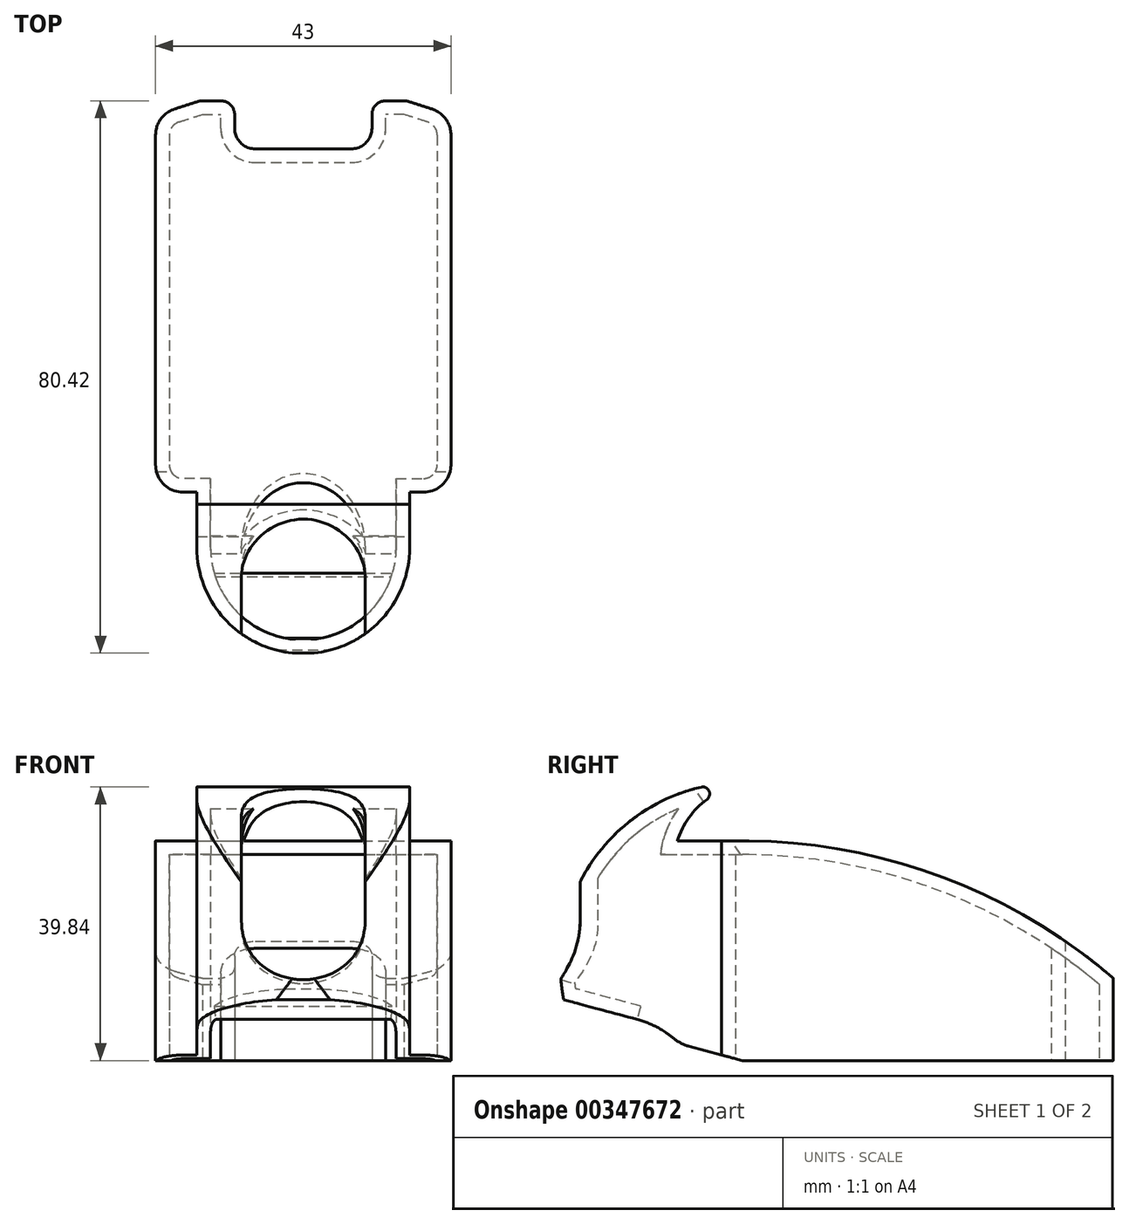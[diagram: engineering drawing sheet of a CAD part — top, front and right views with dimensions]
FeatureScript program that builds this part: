
annotation { "Feature Type Name" : "Feature", "Feature Type Description" : "" }
export const myFeature = defineFeature(function(context is Context, id is Id, definition is map)
    precondition{}
    {
        {
            var Q0;
            Q0=qCreatedBy(makeId("Top.planeOp"),FACE);
            var sketch = newSketch(context, id + "F0", { "sketchPlane" : qUnion([Q0])});
            skArc(sketch, "E0", {"start": v(-18.72, 27.8) * mm, "mid": v(-20.73, 26.36) * mm, "end": v(-21.5, 24) * mm});
            skArc(sketch, "E1.MirrorC", {"start": v(18.72, 27.8) * mm, "mid": v(20.73, 26.36) * mm, "end": v(21.5, 24) * mm});
            skArc(sketch, "E2.MirrorC", {"start": v(-17.5, -28) * mm, "mid": v(-20.33, -26.83) * mm, "end": v(-21.5, -24) * mm});
            skArc(sketch, "E3.MirrorC", {"start": v(17.5, -28) * mm, "mid": v(20.33, -26.83) * mm, "end": v(21.5, -24) * mm});
            skLineSegment(sketch, "E4", {"start": v(-21.5, 24) * mm, "end": v(-21.5, -24) * mm});
            skLineSegment(sketch, "E5", {"start": v(21.5, 24) * mm, "end": v(21.5, -24) * mm});
            skLineSegment(sketch, "E6", {"start": v(-7, 22) * mm, "end": v(7, 22) * mm});
            skLineSegment(sketch, "E7", {"start": v(-10, 25) * mm, "end": v(-10, 27) * mm});
            skLineSegment(sketch, "E8", {"start": v(10, 25) * mm, "end": v(10, 27) * mm});
            skPoint(sketch, "E9.visualSharp", {"position": v(-10, 22) * mm});
            skArc(sketch, "E9.filletArc", {"start": v(-10, 25) * mm, "mid": v(-9.12, 22.88) * mm, "end": v(-7, 22) * mm});
            skPoint(sketch, "E10.visualSharp", {"position": v(10, 22) * mm});
            skArc(sketch, "E10.filletArc", {"start": v(7, 22) * mm, "mid": v(9.12, 22.88) * mm, "end": v(10, 25) * mm});
            skLineSegment(sketch, "E11", {"start": v(-18.72, 27.8) * mm, "end": v(-15.3, 28.9) * mm});
            skLineSegment(sketch, "E12", {"start": v(-14.69, 29) * mm, "end": v(-12, 29) * mm});
            skLineSegment(sketch, "E13", {"start": v(18.72, 27.8) * mm, "end": v(15.3, 28.9) * mm});
            skLineSegment(sketch, "E14", {"start": v(14.69, 29) * mm, "end": v(12, 29) * mm});
            skPoint(sketch, "E15.visualSharp", {"position": v(-10, 29) * mm});
            skArc(sketch, "E15.filletArc", {"start": v(-10, 27) * mm, "mid": v(-10.59, 28.41) * mm, "end": v(-12, 29) * mm});
            skPoint(sketch, "E16.visualSharp", {"position": v(10, 29) * mm});
            skArc(sketch, "E16.filletArc", {"start": v(12, 29) * mm, "mid": v(10.59, 28.41) * mm, "end": v(10, 27) * mm});
            skPoint(sketch, "E17.visualSharp", {"position": v(-15, 29) * mm});
            skArc(sketch, "E17.filletArc", {"start": v(-14.69, 29) * mm, "mid": v(-15, 28.98) * mm, "end": v(-15.3, 28.9) * mm});
            skPoint(sketch, "E18.visualSharp", {"position": v(15, 29) * mm});
            skArc(sketch, "E18.filletArc", {"start": v(15.3, 28.9) * mm, "mid": v(15, 28.98) * mm, "end": v(14.69, 29) * mm});
            skLineSegment(sketch, "E19", {"start": v(-15.5, -28) * mm, "end": v(-15.5, -36) * mm});
            skLineSegment(sketch, "E20", {"start": v(15.5, -28) * mm, "end": v(15.5, -36) * mm});
            skLineSegment(sketch, "E21", {"start": v(-17.5, -28) * mm, "end": v(-15.5, -28) * mm});
            skLineSegment(sketch, "E22", {"start": v(17.5, -28) * mm, "end": v(15.5, -28) * mm});
            skArc(sketch, "E23", {"start": v(-15.5, -36) * mm, "mid": v(0, -51.5) * mm, "end": v(15.5, -36) * mm});
            skSolve(sketch);
        }
        {
            var Q0;
            Q0=makeQuery(id+"F0.imprint","IMPRINT",FACE,{"disambiguationData":[TD([[makeQuery(id+"F0.imprint","IMPRINT",EDGE,{"derivedFrom":sQuery(id+"F0.wireOp",EDGE,"E0")}),1.0]])]});
            extrude(context, id + "F1", {"entities" : qUnion([Q0]), "depth" : 32 * mm});
        }
        {
            var Q0;
            Q0=qCreatedBy(makeId("Right.planeOp"),FACE);
            var sketch = newSketch(context, id + "F2", { "sketchPlane" : qUnion([Q0])});
            skLineSegment(sketch, "E24", {"start": v(-25, 0) * mm, "end": v(-32.73, 2.07) * mm});
            skArc(sketch, "E25", {"start": v(-35, 3.25) * mm, "mid": v(-33.93, 2.54) * mm, "end": v(-32.73, 2.07) * mm});
            skArc(sketch, "E26", {"start": v(-35, 3.25) * mm, "mid": v(-37.51, 4.9) * mm, "end": v(-40.32, 6) * mm});
            skLineSegment(sketch, "E27", {"start": v(-40.32, 6) * mm, "end": v(-59, 11) * mm});
            skLineSegment(sketch, "E28", {"start": v(-59, 11) * mm, "end": v(-59, 0) * mm});
            skLineSegment(sketch, "E29", {"start": v(-59, 0) * mm, "end": v(-25, 0) * mm});
            skSolve(sketch);
        }
        {
            var Q0;
            Q0=makeQuery(id+"F2.imprint","IMPRINT",FACE,{"disambiguationData":[TD([[makeQuery(id+"F2.imprint","IMPRINT",EDGE,{"derivedFrom":sQuery(id+"F2.wireOp",EDGE,"E24")}),1.0]])]});
            extrude(context, id + "F3", {"entities" : qUnion([Q0]), "operationType" : NewBodyOperationType.REMOVE, "endBound" : BoundingType.SYMMETRIC, "oppositeDirection" : true, "depth" : 100 * mm});
        }
        {
            var Q0;
            Q0=qCreatedBy(makeId("Right.planeOp"),FACE);
            var sketch = newSketch(context, id + "F4", { "sketchPlane" : qUnion([Q0])});
            skArc(sketch, "E30", {"start": v(-43.47, 33) * mm, "mid": v(-50.57, 20.97) * mm, "end": v(-50.56, 7) * mm});
            skLineSegment(sketch, "E31", {"start": v(-43.47, 33) * mm, "end": v(-60, 33) * mm});
            skLineSegment(sketch, "E32", {"start": v(-60, 33) * mm, "end": v(-60, 7) * mm});
            skLineSegment(sketch, "E33", {"start": v(-60, 7) * mm, "end": v(-50.56, 7) * mm});
            skSolve(sketch);
        }
        {
            var Q0;
            Q0=makeQuery(id+"F4.imprint","IMPRINT",FACE,{"disambiguationData":[TD([[makeQuery(id+"F4.imprint","IMPRINT",EDGE,{"derivedFrom":sQuery(id+"F4.wireOp",EDGE,"E30")}),-1.0]])]});
            extrude(context, id + "F5", {"entities" : qUnion([Q0]), "operationType" : NewBodyOperationType.REMOVE, "endBound" : BoundingType.SYMMETRIC, "oppositeDirection" : true, "depth" : 100 * mm});
        }
        {
            var Q0;
            Q0=qCreatedBy(makeId("Right.planeOp"),FACE);
            var sketch = newSketch(context, id + "F6", { "sketchPlane" : qUnion([Q0])});
            skArc(sketch, "E34", {"start": v(29, 12) * mm, "mid": v(3.8, 26.84) * mm, "end": v(-25, 32) * mm});
            skLineSegment(sketch, "E35", {"start": v(29, 12) * mm, "end": v(29, 32) * mm});
            skLineSegment(sketch, "E36", {"start": v(29, 32) * mm, "end": v(-25, 32) * mm});
            skSolve(sketch);
        }
        {
            var Q0;
            Q0 = qSketchRegion(id + "F6", true);
            extrude(context, id + "F7", {"entities" : qUnion([Q0]), "operationType" : NewBodyOperationType.REMOVE, "endBound" : BoundingType.SYMMETRIC, "oppositeDirection" : true, "depth" : 50 * mm});
        }
        {
            var Q0;
            Q0=makeQuery(id+"F1.opExtrude","CAP_FACE",FACE,{"disambiguationData":[OSD([sQuery(id+"F0.wireOp",EDGE,"E0"),sQuery(id+"F0.wireOp",EDGE,"E1.MirrorC"),sQuery(id+"F0.wireOp",EDGE,"E2.MirrorC"),sQuery(id+"F0.wireOp",EDGE,"E3.MirrorC"),sQuery(id+"F0.wireOp",EDGE,"E4"),sQuery(id+"F0.wireOp",EDGE,"E5"),sQuery(id+"F0.wireOp",EDGE,"E6"),sQuery(id+"F0.wireOp",EDGE,"E7"),sQuery(id+"F0.wireOp",EDGE,"E8"),sQuery(id+"F0.wireOp",EDGE,"E9.filletArc"),sQuery(id+"F0.wireOp",EDGE,"E10.filletArc"),sQuery(id+"F0.wireOp",EDGE,"E11"),sQuery(id+"F0.wireOp",EDGE,"E12"),sQuery(id+"F0.wireOp",EDGE,"E13"),sQuery(id+"F0.wireOp",EDGE,"E14"),sQuery(id+"F0.wireOp",EDGE,"E15.filletArc"),sQuery(id+"F0.wireOp",EDGE,"E16.filletArc"),sQuery(id+"F0.wireOp",EDGE,"E17.filletArc"),sQuery(id+"F0.wireOp",EDGE,"E18.filletArc"),sQuery(id+"F0.wireOp",EDGE,"E19"),sQuery(id+"F0.wireOp",EDGE,"E20"),sQuery(id+"F0.wireOp",EDGE,"E21"),sQuery(id+"F0.wireOp",EDGE,"E22"),sQuery(id+"F0.wireOp",EDGE,"E23")])],"isStart":false});
            extrude(context, id + "F8", {"entities" : qUnion([Q0]), "operationType" : NewBodyOperationType.ADD, "depth" : 10 * mm});
        }
        {
            var Q0;
            Q0=qCreatedBy(makeId("Right.planeOp"),FACE);
            var sketch = newSketch(context, id + "F9", { "sketchPlane" : qUnion([Q0])});
            skArc(sketch, "E37", {"start": v(-30.97, 39.82) * mm, "mid": v(-38.3, 36.92) * mm, "end": v(-44.45, 32) * mm});
            skArc(sketch, "E38", {"start": v(-30.15, 38.04) * mm, "mid": v(-32.78, 35.36) * mm, "end": v(-34.45, 32) * mm});
            skLineSegment(sketch, "E39", {"start": v(-34.45, 32) * mm, "end": v(-44.45, 32) * mm, "construction": true});
            skLineSegment(sketch, "E40", {"start": v(-44.45, 32) * mm, "end": v(-25, 14) * mm, "construction": true});
            skPoint(sketch, "E41.visualSharp", {"position": v(-22.71, 40.4) * mm});
            skArc(sketch, "E41.filletArc", {"start": v(-30.15, 38.04) * mm, "mid": v(-29.84, 39.26) * mm, "end": v(-30.97, 39.82) * mm});
            skLineSegment(sketch, "E42", {"start": v(-34.45, 32) * mm, "end": v(-22.45, 32) * mm});
            skLineSegment(sketch, "E43", {"start": v(-22.45, 32) * mm, "end": v(-22.45, 44) * mm});
            skLineSegment(sketch, "E44", {"start": v(-22.45, 44) * mm, "end": v(-47.45, 44) * mm});
            skLineSegment(sketch, "E45", {"start": v(-47.45, 44) * mm, "end": v(-47.45, 32) * mm});
            skLineSegment(sketch, "E46", {"start": v(-47.45, 32) * mm, "end": v(-44.45, 32) * mm});
            skSolve(sketch);
        }
        {
            var Q0;
            Q0=makeQuery(id+"F9.imprint","IMPRINT",FACE,{"disambiguationData":[TD([[makeQuery(id+"F9.imprint","IMPRINT",EDGE,{"derivedFrom":sQuery(id+"F9.wireOp",EDGE,"E37")}),-1.0]])]});
            extrude(context, id + "F10", {"entities" : qUnion([Q0]), "operationType" : NewBodyOperationType.REMOVE, "endBound" : BoundingType.SYMMETRIC, "oppositeDirection" : true, "depth" : 50 * mm});
        }
        {
            var Q0;
            Q0=makeQuery(id+"F1.opExtrude","CAP_FACE",FACE,{"disambiguationData":[OSD([sQuery(id+"F0.wireOp",EDGE,"E0"),sQuery(id+"F0.wireOp",EDGE,"E1.MirrorC"),sQuery(id+"F0.wireOp",EDGE,"E2.MirrorC"),sQuery(id+"F0.wireOp",EDGE,"E3.MirrorC"),sQuery(id+"F0.wireOp",EDGE,"E4"),sQuery(id+"F0.wireOp",EDGE,"E5"),sQuery(id+"F0.wireOp",EDGE,"E6"),sQuery(id+"F0.wireOp",EDGE,"E7"),sQuery(id+"F0.wireOp",EDGE,"E8"),sQuery(id+"F0.wireOp",EDGE,"E9.filletArc"),sQuery(id+"F0.wireOp",EDGE,"E10.filletArc"),sQuery(id+"F0.wireOp",EDGE,"E11"),sQuery(id+"F0.wireOp",EDGE,"E12"),sQuery(id+"F0.wireOp",EDGE,"E13"),sQuery(id+"F0.wireOp",EDGE,"E14"),sQuery(id+"F0.wireOp",EDGE,"E15.filletArc"),sQuery(id+"F0.wireOp",EDGE,"E16.filletArc"),sQuery(id+"F0.wireOp",EDGE,"E17.filletArc"),sQuery(id+"F0.wireOp",EDGE,"E18.filletArc"),sQuery(id+"F0.wireOp",EDGE,"E19"),sQuery(id+"F0.wireOp",EDGE,"E20"),sQuery(id+"F0.wireOp",EDGE,"E21"),sQuery(id+"F0.wireOp",EDGE,"E22"),sQuery(id+"F0.wireOp",EDGE,"E23")])],"isStart":true});
            var Q1;
            Q1=makeQuery(id+"F3.boolean.opBoolean","COPY",FACE,{"derivedFrom":makeQuery(id+"F3.opExtrude","SWEPT_FACE",FACE,{"disambiguationData":[OSD([sQuery(id+"F2.wireOp",EDGE,"E24")])]})});
            var Q2;
            Q2=makeQuery(id+"F3.boolean.opBoolean","COPY",FACE,{"derivedFrom":makeQuery(id+"F3.opExtrude","SWEPT_FACE",FACE,{"disambiguationData":[OSD([sQuery(id+"F2.wireOp",EDGE,"E25")])]})});
            var Q3;
            Q3=makeQuery(id+"F3.boolean.opBoolean","COPY",FACE,{"derivedFrom":makeQuery(id+"F3.opExtrude","SWEPT_FACE",FACE,{"disambiguationData":[OSD([sQuery(id+"F2.wireOp",EDGE,"E26")])]})});
            shell(context, id + "F11", {"entities" : qUnion([Q0, Q1, Q2, Q3]), "thickness" : 2 * mm});
        }
        {
            var Q0;
            Q0=qCreatedBy(makeId("Right.planeOp"),FACE);
            var sketch = newSketch(context, id + "F12", { "sketchPlane" : qUnion([Q0])});
            skLineSegment(sketch, "E47", {"start": v(-25, 14) * mm, "end": v(-63.64, 24.35) * mm, "construction": true});
            skLineSegment(sketch, "E48", {"start": v(-25, 14) * mm, "end": v(-47.94, 46.77) * mm, "construction": true});
            skLineSegment(sketch, "E49", {"start": v(-25, 14) * mm, "end": v(-27.33, 5.3) * mm});
            skLineSegment(sketch, "E50", {"start": v(-27.33, 5.3) * mm, "end": v(-61.14, 14.37) * mm});
            skLineSegment(sketch, "E51", {"start": v(-25, 14) * mm, "end": v(-17.63, 19.16) * mm});
            skLineSegment(sketch, "E52", {"start": v(-17.63, 19.16) * mm, "end": v(-37.94, 48.17) * mm});
            skLineSegment(sketch, "E53", {"start": v(-37.94, 48.17) * mm, "end": v(-61.14, 14.37) * mm});
            skSolve(sketch);
        }
        {
            var Q0;
            Q0=makeQuery(id+"F12.imprint","IMPRINT",FACE,{"disambiguationData":[TD([[makeQuery(id+"F12.imprint","IMPRINT",EDGE,{"derivedFrom":sQuery(id+"F12.wireOp",EDGE,"E49")}),-1.0]])]});
            extrude(context, id + "F13", {"entities" : qUnion([Q0]), "operationType" : NewBodyOperationType.REMOVE, "endBound" : BoundingType.SYMMETRIC, "oppositeDirection" : true, "depth" : 18 * mm});
        }
        {
            var Q0;
            {var subQ0=sQuery(id+"F9.wireOp",EDGE,"E42");var subQ1=sQuery(id+"F12.wireOp",EDGE,"E52");Q0=makeQuery(id+"F13.boolean.opBoolean","COPY",EDGE,{"disambiguationData":[TD([makeQuery(id+"F10.boolean.opBoolean","COPY",FACE,{"derivedFrom":makeQuery(id+"F10.opExtrude","SWEPT_FACE",FACE,{"disambiguationData":[OSD([subQ0])]})})])],"derivedFrom":makeQuery(id+"F13.opExtrude","CAP_EDGE",EDGE,{"disambiguationData":[OSD([subQ1])],"isStart":false})});}
            var Q1;
            {var subQ0=sQuery(id+"F9.wireOp",EDGE,"E42");var subQ1=sQuery(id+"F12.wireOp",EDGE,"E52");Q1=makeQuery(id+"F13.boolean.opBoolean","COPY",EDGE,{"disambiguationData":[TD([makeQuery(id+"F10.boolean.opBoolean","COPY",FACE,{"derivedFrom":makeQuery(id+"F10.opExtrude","SWEPT_FACE",FACE,{"disambiguationData":[OSD([subQ0])]})})])],"derivedFrom":makeQuery(id+"F13.opExtrude","CAP_EDGE",EDGE,{"disambiguationData":[OSD([subQ1])],"isStart":true})});}
            var Q2;
            Q2=makeQuery(id+"F13.boolean.opBoolean","COPY",EDGE,{"derivedFrom":makeQuery(id+"F13.opExtrude","CAP_EDGE",EDGE,{"disambiguationData":[OSD([sQuery(id+"F12.wireOp",EDGE,"E50")])],"isStart":false})});
            var Q3;
            Q3=makeQuery(id+"F13.boolean.opBoolean","COPY",EDGE,{"derivedFrom":makeQuery(id+"F13.opExtrude","CAP_EDGE",EDGE,{"disambiguationData":[OSD([sQuery(id+"F12.wireOp",EDGE,"E50")])],"isStart":true})});
            fillet(context, id + "F14", {"entities" : qUnion([Q0, Q1, Q2, Q3]), "radius" : 9 * mm, "tangentPropagation" : true, "allowEdgeOverflow" : false});
        }
    });
